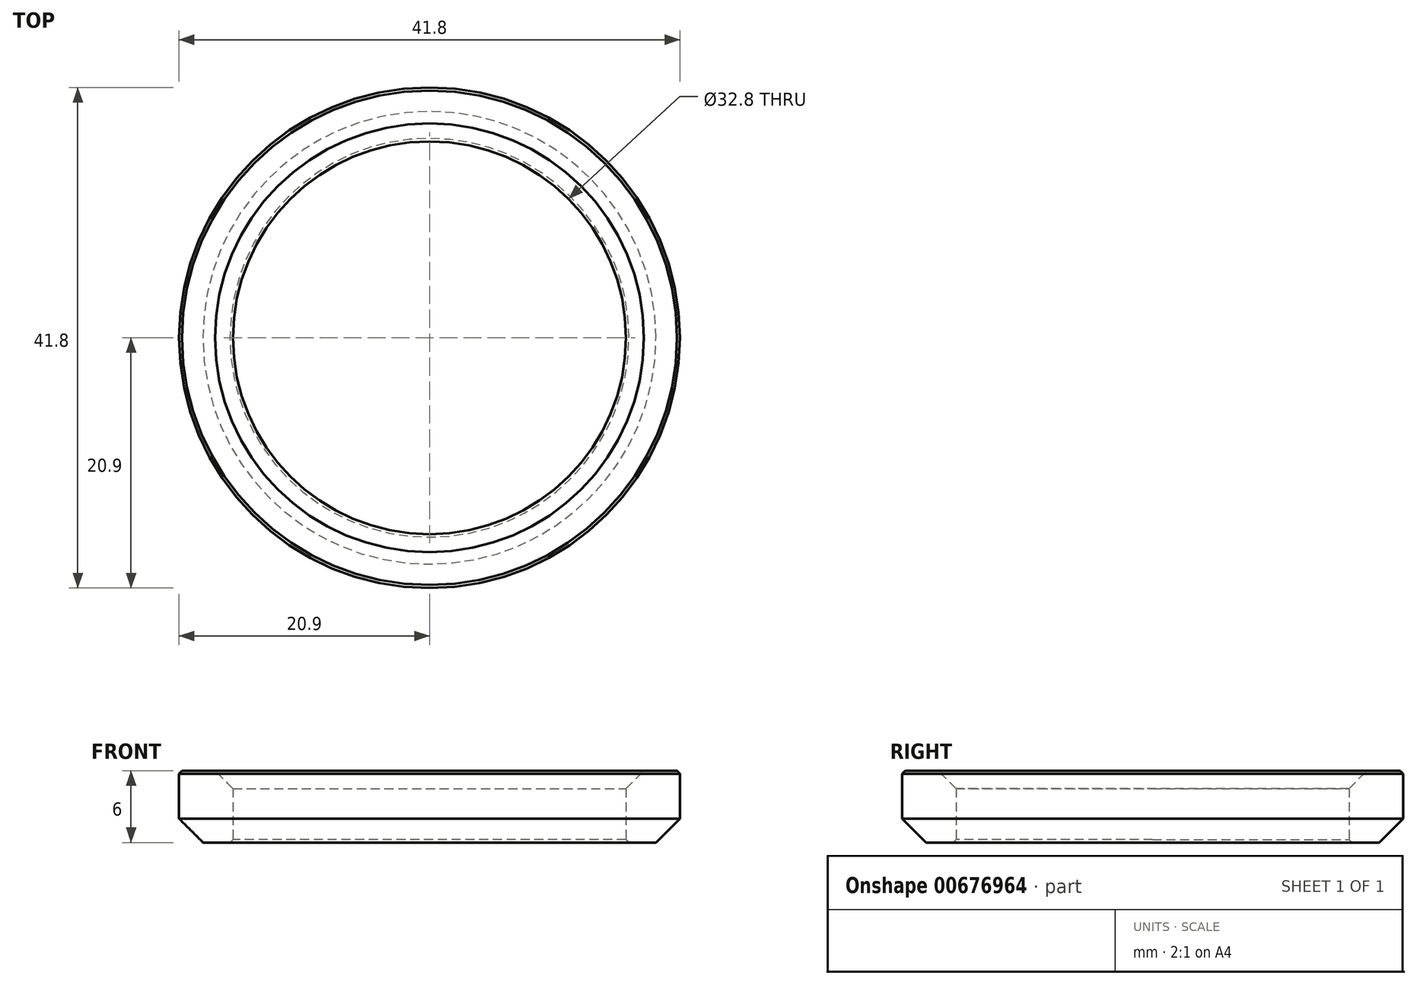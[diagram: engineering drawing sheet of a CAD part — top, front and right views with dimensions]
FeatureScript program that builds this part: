
annotation { "Feature Type Name" : "Feature", "Feature Type Description" : "" }
export const myFeature = defineFeature(function(context is Context, id is Id, definition is map)
    precondition{}
    {
        {
            var Q0;
            Q0=qCreatedBy(makeId("Right.planeOp"),FACE);
            var sketch = newSketch(context, id + "F0", { "sketchPlane" : qUnion([Q0])});
            skLineSegment(sketch, "E0", {"start": v(0, 0) * mm, "end": v(16.4, 0) * mm});
            skLineSegment(sketch, "E1", {"start": v(16.4, 0) * mm, "end": v(16.4, 6) * mm, "construction": true});
            skLineSegment(sketch, "E2", {"start": v(16.4, 6) * mm, "end": v(20.9, 6) * mm, "construction": true});
            skLineSegment(sketch, "E3", {"start": v(20.9, 6) * mm, "end": v(20.9, 0) * mm, "construction": true});
            skLineSegment(sketch, "E4", {"start": v(20.9, 0) * mm, "end": v(16.4, 0) * mm, "construction": true});
            skLineSegment(sketch, "E5", {"start": v(16.4, 4.5) * mm, "end": v(17.9, 6) * mm});
            skLineSegment(sketch, "E6", {"start": v(18.9, 0) * mm, "end": v(20.9, 2) * mm});
            skLineSegment(sketch, "E7", {"start": v(16.4, 4.5) * mm, "end": v(16.4, 0) * mm});
            skLineSegment(sketch, "E8", {"start": v(18.9, 0) * mm, "end": v(16.4, 0) * mm});
            skLineSegment(sketch, "E9", {"start": v(20.9, 2) * mm, "end": v(20.9, 6) * mm});
            skLineSegment(sketch, "E10", {"start": v(20.9, 6) * mm, "end": v(17.9, 6) * mm});
            skLineSegment(sketch, "E11", {"start": v(0, 0) * mm, "end": v(0, 12.73) * mm});
            skSolve(sketch);
        }
        {
            var Q0;
            Q0 = qSketchRegion(id + "F0", true);
            var Q1;
            Q1=sQuery(id+"F0.wireOp",EDGE,"E11");
            revolve(context, id + "F1", {"entities" : qUnion([Q0]), "axis" : qUnion([Q1]), "revolveType" : RevolveType.FULL});
        }
        {
            var Q0;
            Q0=makeQuery(id+"F1.opRevolve","SWEPT_EDGE",EDGE,{"disambiguationData":[OSD([sQuery(id+"F0.wireOp",EDGE,"E9"),sQuery(id+"F0.wireOp",EDGE,"E10")])]});
            chamfer(context, id + "F2", {"entities" : qUnion([Q0]), "width" : .25 * mm, "tangentPropagation" : true});
        }
        {
            var Q0;
            Q0=makeQuery(id+"F1.opRevolve","SWEPT_EDGE",EDGE,{"disambiguationData":[OSD([sQuery(id+"F0.wireOp",EDGE,"E7"),sQuery(id+"F0.wireOp",EDGE,"E8")])]});
            chamfer(context, id + "F3", {"entities" : qUnion([Q0]), "width" : .25 * mm, "tangentPropagation" : true});
        }
    });
